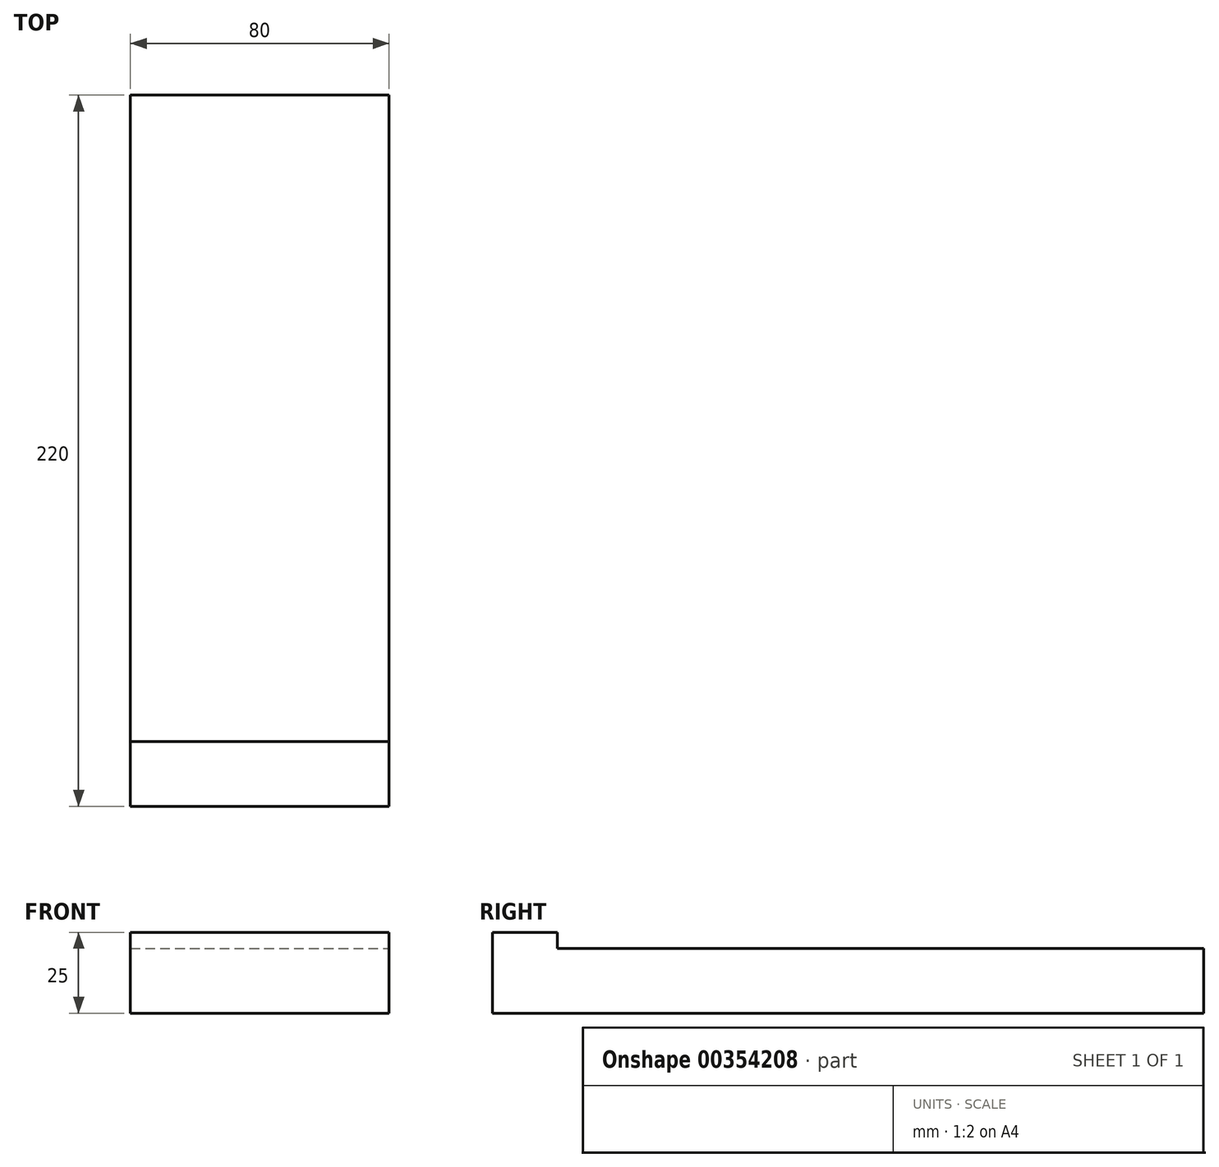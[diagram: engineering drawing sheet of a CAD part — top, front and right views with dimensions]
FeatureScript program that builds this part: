
annotation { "Feature Type Name" : "Feature", "Feature Type Description" : "" }
export const myFeature = defineFeature(function(context is Context, id is Id, definition is map)
    precondition{}
    {
        {
            var Q0;
            Q0=qCreatedBy(makeId("Top.planeOp"),FACE);
            var sketch = newSketch(context, id + "F0", { "sketchPlane" : qUnion([Q0])});
            skLineSegment(sketch, "E0.bottom", {"start": v(0, 0) * mm, "end": v(20, 0) * mm});
            skLineSegment(sketch, "E0.top", {"start": v(0, 20) * mm, "end": v(20, 20) * mm});
            skLineSegment(sketch, "E0.left", {"start": v(0, 0) * mm, "end": v(0, 20) * mm});
            skLineSegment(sketch, "E0.right", {"start": v(20, 0) * mm, "end": v(20, 20) * mm});
            skSolve(sketch);
        }
        {
            var Q0;
            Q0=makeQuery(id+"F0.imprint","IMPRINT",FACE,{"disambiguationData":[TD([[makeQuery(id+"F0.imprint","IMPRINT",EDGE,{"derivedFrom":sQuery(id+"F0.wireOp",EDGE,"E0.bottom")}),1.0]])]});
            extrude(context, id + "F1", {"entities" : qUnion([Q0]), "depth" : 20 * mm});
        }
        {
            var Q0;
            Q0=makeQuery(id+"F1.opExtrude","SWEPT_FACE",FACE,{"disambiguationData":[OSD([sQuery(id+"F0.wireOp",EDGE,"E0.top")])]});
            extrude(context, id + "F2", {"entities" : qUnion([Q0]), "depth" : 200 * mm});
        }
        {
            var Q0;
            Q0=makeQuery(id+"F1.opExtrude","CAP_FACE",FACE,{"disambiguationData":[OSD([sQuery(id+"F0.wireOp",EDGE,"E0.bottom"),sQuery(id+"F0.wireOp",EDGE,"E0.top"),sQuery(id+"F0.wireOp",EDGE,"E0.left"),sQuery(id+"F0.wireOp",EDGE,"E0.right")])],"isStart":false});
            extrude(context, id + "F3", {"entities" : qUnion([Q0]), "operationType" : NewBodyOperationType.ADD, "depth" : 5 * mm});
        }
        {
            var Q0;
            Q0=makeQuery(id+"F2.opExtrude","SWEPT_FACE",FACE,{"disambiguationData":[OSD([sQuery(id+"F0.wireOp",EDGE,"E0.top"),sQuery(id+"F0.wireOp",EDGE,"E0.right")])]});
            extrude(context, id + "F4", {"entities" : qUnion([Q0]), "operationType" : NewBodyOperationType.ADD, "depth" : 20 * mm});
        }
        {
            var Q0;
            Q0=makeQuery(id+"F4.opExtrude","CAP_FACE",FACE,{"disambiguationData":[OSD([sQuery(id+"F0.wireOp",EDGE,"E0.top"),sQuery(id+"F0.wireOp",EDGE,"E0.right")])],"isStart":false});
            extrude(context, id + "F5", {"entities" : qUnion([Q0]), "operationType" : NewBodyOperationType.ADD, "depth" : 40 * mm});
        }
    });
